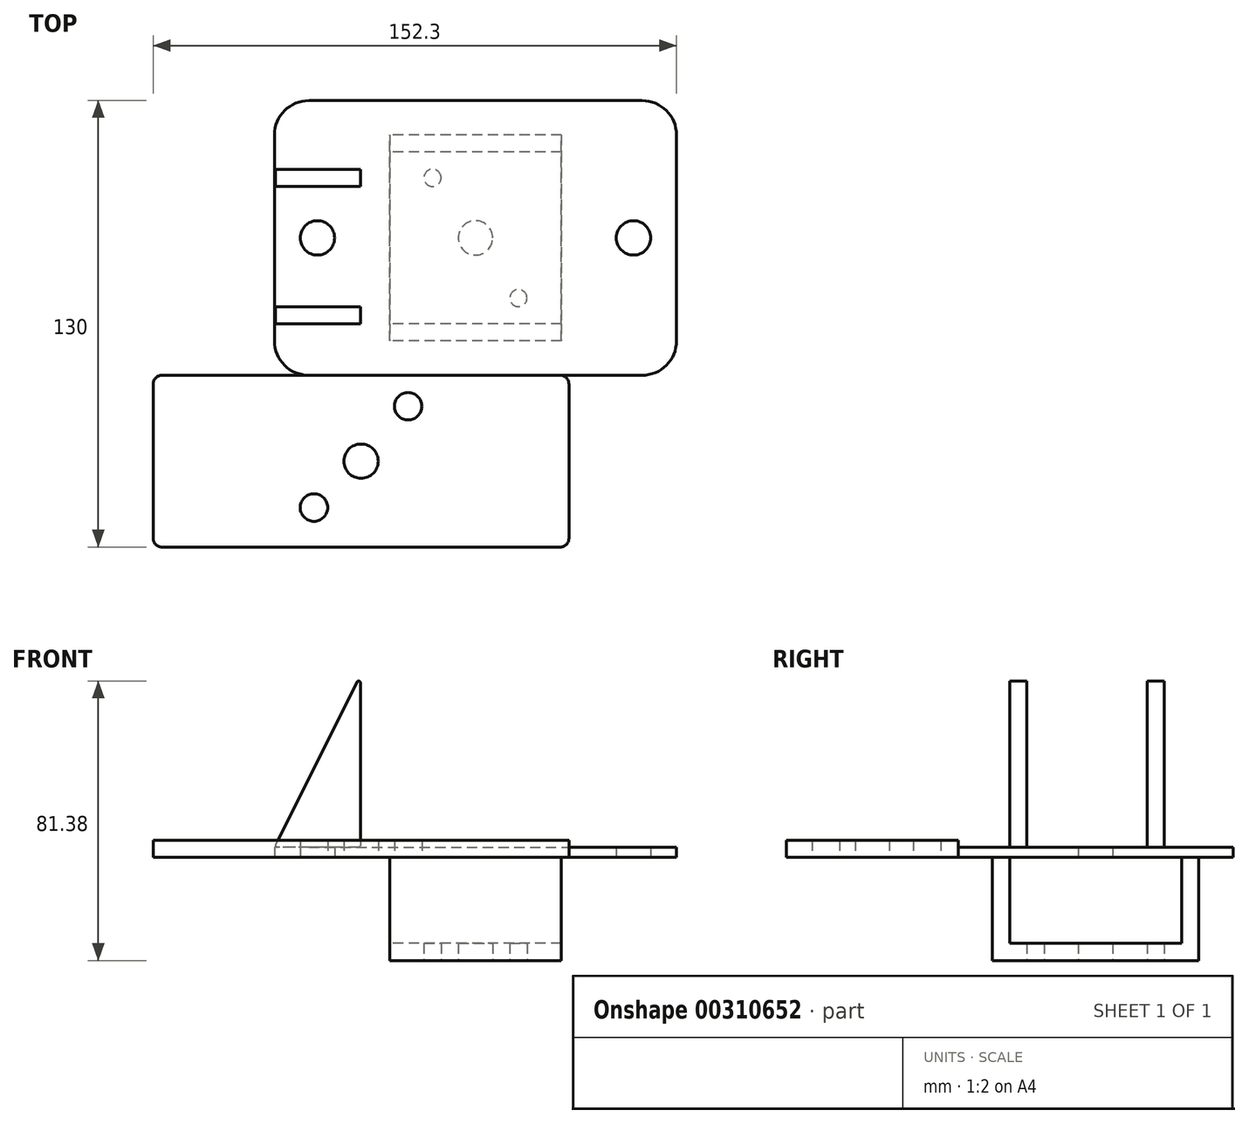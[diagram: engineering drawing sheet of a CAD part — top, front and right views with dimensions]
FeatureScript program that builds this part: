
annotation { "Feature Type Name" : "Feature", "Feature Type Description" : "" }
export const myFeature = defineFeature(function(context is Context, id is Id, definition is map)
    precondition{}
    {
        {
            var Q0;
            Q0=qCreatedBy(makeId("Top.planeOp"),FACE);
            var sketch = newSketch(context, id + "F0", { "sketchPlane" : qUnion([Q0])});
            skLineSegment(sketch, "E0.bottom", {"start": v(10, 0) * mm, "end": v(107, 0) * mm});
            skLineSegment(sketch, "E0.top", {"start": v(10, 80) * mm, "end": v(107, 80) * mm});
            skLineSegment(sketch, "E0.left", {"start": v(0, 10) * mm, "end": v(0, 70) * mm});
            skLineSegment(sketch, "E0.right", {"start": v(117, 10) * mm, "end": v(117, 70) * mm});
            skCircle(sketch, "E1", {"center": v(12.5, 40) * mm, "radius": 5 * mm});
            skCircle(sketch, "E2", {"center": v(104.5, 40) * mm, "radius": 5 * mm});
            skPoint(sketch, "E3", {"position": v(0, 40) * mm});
            skPoint(sketch, "E4.visualSharp", {"position": v(0, 80) * mm});
            skArc(sketch, "E4.filletArc", {"start": v(10, 80) * mm, "mid": v(2.93, 77.07) * mm, "end": v(0, 70) * mm});
            skPoint(sketch, "E5.visualSharp", {"position": v(117, 80) * mm});
            skArc(sketch, "E5.filletArc", {"start": v(117, 70) * mm, "mid": v(114.07, 77.07) * mm, "end": v(107, 80) * mm});
            skPoint(sketch, "E6.visualSharp", {"position": v(117, 0) * mm});
            skArc(sketch, "E6.filletArc", {"start": v(107, 0) * mm, "mid": v(114.07, 2.93) * mm, "end": v(117, 10) * mm});
            skPoint(sketch, "E7.visualSharp", {"position": v(0, 0) * mm});
            skArc(sketch, "E7.filletArc", {"start": v(0, 10) * mm, "mid": v(2.93, 2.93) * mm, "end": v(10, 0) * mm});
            skSolve(sketch);
        }
        {
            var Q0;
            Q0 = qSketchRegion(id + "F0", true);
            extrude(context, id + "F1", {"entities" : qUnion([Q0]), "depth" : 3 * mm});
        }
        {
            var Q0;
            Q0=qCreatedBy(makeId("Right.planeOp"),FACE);
            var sketch = newSketch(context, id + "F2", { "sketchPlane" : qUnion([Q0])});
            skLineSegment(sketch, "E8", {"start": v(10, 0) * mm, "end": v(10, -30) * mm});
            skLineSegment(sketch, "E9", {"start": v(10, -30) * mm, "end": v(70, -30) * mm});
            skLineSegment(sketch, "E10", {"start": v(70, -30) * mm, "end": v(70, 0) * mm});
            skLineSegment(sketch, "E11", {"start": v(70, 0) * mm, "end": v(65, 0) * mm});
            skLineSegment(sketch, "E12", {"start": v(65, 0) * mm, "end": v(65, -25) * mm});
            skLineSegment(sketch, "E13", {"start": v(65, -25) * mm, "end": v(15, -25) * mm});
            skLineSegment(sketch, "E14", {"start": v(15, -25) * mm, "end": v(15, 0) * mm});
            skLineSegment(sketch, "E15", {"start": v(15, 0) * mm, "end": v(10, 0) * mm});
            skSolve(sketch);
        }
        {
            var Q0;
            Q0 = qSketchRegion(id + "F2", true);
            extrude(context, id + "F3", {"entities" : qUnion([Q0]), "depth" : 50 * mm});
        }
        {
            var Q0;
            Q0=makeQuery(id+"F3.opExtrude","SWEPT_BODY",BODY,{"disambiguationData":[OSD([sQuery(id+"F2.wireOp",EDGE,"E8"),sQuery(id+"F2.wireOp",EDGE,"E9"),sQuery(id+"F2.wireOp",EDGE,"E10"),sQuery(id+"F2.wireOp",EDGE,"E11"),sQuery(id+"F2.wireOp",EDGE,"E12"),sQuery(id+"F2.wireOp",EDGE,"E13"),sQuery(id+"F2.wireOp",EDGE,"E14"),sQuery(id+"F2.wireOp",EDGE,"E15")])]});
            transform(context, id + "F4", {"entities" : qUnion([Q0]), "transformType" : TransformType.TRANSLATION_3D, "dx" : 33.5 * mm, "dy" : 0 * mm, "dz" : 0 * mm, "makeCopy" : false});
        }
        {
            var Q0;
            Q0=makeQuery(id+"F3.opExtrude","SWEPT_FACE",FACE,{"disambiguationData":[OSD([sQuery(id+"F2.wireOp",EDGE,"E9")])]});
            var sketch = newSketch(context, id + "F5", { "sketchPlane" : qUnion([Q0])});
            skCircle(sketch, "E16", {"center": v(58.5, -40) * mm, "radius": 5 * mm});
            skPoint(sketch, "E17", {"position": v(33.5, -40) * mm});
            skPoint(sketch, "E18", {"position": v(58.5, -10) * mm});
            skCircle(sketch, "E19", {"center": v(46, -57.5) * mm, "radius": 2.5 * mm});
            skCircle(sketch, "E20", {"center": v(71, -22.5) * mm, "radius": 2.5 * mm});
            skSolve(sketch);
        }
        {
            var Q0;
            Q0 = qSketchRegion(id + "F5", true);
            extrude(context, id + "F6", {"entities" : qUnion([Q0]), "operationType" : NewBodyOperationType.REMOVE, "oppositeDirection" : true, "depth" : 25 * mm});
        }
        {
            var Q0;
            Q0=qCreatedBy(makeId("Front.planeOp"),FACE);
            var sketch = newSketch(context, id + "F7", { "sketchPlane" : qUnion([Q0])});
            skLineSegment(sketch, "E21", {"start": v(25, 50.88) * mm, "end": v(25, 3.5) * mm});
            skLineSegment(sketch, "E22", {"start": v(24.5, 3) * mm, "end": v(0.8, 3) * mm});
            skLineSegment(sketch, "E23", {"start": v(0.36, 3.72) * mm, "end": v(24.05, 51.1) * mm});
            skPoint(sketch, "E24.visualSharp", {"position": v(25, 53) * mm});
            skArc(sketch, "E24.filletArc", {"start": v(25, 50.88) * mm, "mid": v(24.61, 51.37) * mm, "end": v(24.05, 51.1) * mm});
            skPoint(sketch, "E25.visualSharp", {"position": v(0, 3) * mm});
            skArc(sketch, "E25.filletArc", {"start": v(0.36, 3.72) * mm, "mid": v(0.38, 3.24) * mm, "end": v(0.8, 3) * mm});
            skPoint(sketch, "E26.visualSharp", {"position": v(25, 3) * mm});
            skArc(sketch, "E26.filletArc", {"start": v(24.5, 3) * mm, "mid": v(24.85, 3.15) * mm, "end": v(25, 3.5) * mm});
            skSolve(sketch);
        }
        {
            var Q0;
            Q0 = qSketchRegion(id + "F7", true);
            extrude(context, id + "F8", {"entities" : qUnion([Q0]), "depth" : 5 * mm});
        }
        {
            var Q0;
            Q0=makeQuery(id+"F8.opExtrude","SWEPT_BODY",BODY,{"disambiguationData":[OSD([sQuery(id+"F7.wireOp",EDGE,"E21"),sQuery(id+"F7.wireOp",EDGE,"E22"),sQuery(id+"F7.wireOp",EDGE,"E23"),sQuery(id+"F7.wireOp",EDGE,"E24.filletArc"),sQuery(id+"F7.wireOp",EDGE,"E25.filletArc"),sQuery(id+"F7.wireOp",EDGE,"E26.filletArc")])]});
            transform(context, id + "F9", {"entities" : qUnion([Q0]), "transformType" : TransformType.TRANSLATION_3D, "dx" : 0 * mm, "dy" : 20 * mm, "dz" : 0 * mm, "makeCopy" : false});
        }
        {
            var Q0;
            Q0=makeQuery(id+"F8.opExtrude","SWEPT_BODY",BODY,{"disambiguationData":[OSD([sQuery(id+"F7.wireOp",EDGE,"E21"),sQuery(id+"F7.wireOp",EDGE,"E22"),sQuery(id+"F7.wireOp",EDGE,"E23"),sQuery(id+"F7.wireOp",EDGE,"E24.filletArc"),sQuery(id+"F7.wireOp",EDGE,"E25.filletArc"),sQuery(id+"F7.wireOp",EDGE,"E26.filletArc")])]});
            transform(context, id + "F10", {"entities" : qUnion([Q0]), "transformType" : TransformType.TRANSLATION_3D, "dx" : 0 * mm, "dy" : 40 * mm, "dz" : 0 * mm, "makeCopy" : true});
        }
        {
            var Q0;
            Q0=qCreatedBy(makeId("Top.planeOp"),FACE);
            var sketch = newSketch(context, id + "F11", { "sketchPlane" : qUnion([Q0])});
            skLineSegment(sketch, "E27.bottom", {"start": v(0, 0) * mm, "end": v(50.4, 0) * mm});
            skLineSegment(sketch, "E27.top", {"start": v(0, -50) * mm, "end": v(50.4, -50) * mm});
            skLineSegment(sketch, "E27.left", {"start": v(0, 0) * mm, "end": v(0, -50) * mm});
            skLineSegment(sketch, "E27.right", {"start": v(50.4, 0) * mm, "end": v(50.4, -50) * mm});
            skCircle(sketch, "E28", {"center": v(25.2, -25) * mm, "radius": 5 * mm});
            skPoint(sketch, "E29", {"position": v(25.2, -50) * mm});
            skPoint(sketch, "E30", {"position": v(0, -25) * mm});
            skLineSegment(sketch, "E31.bottom", {"start": v(0, 0) * mm, "end": v(-32.8, 0) * mm});
            skLineSegment(sketch, "E31.top", {"start": v(0, -50) * mm, "end": v(-32.8, -50) * mm});
            skLineSegment(sketch, "E31.right", {"start": v(-35.3, -2.5) * mm, "end": v(-35.3, -47.5) * mm});
            skLineSegment(sketch, "E32.bottom", {"start": v(50.4, 0) * mm, "end": v(83.2, 0) * mm});
            skLineSegment(sketch, "E32.top", {"start": v(50.4, -50) * mm, "end": v(83.2, -50) * mm});
            skLineSegment(sketch, "E32.right", {"start": v(85.7, -2.5) * mm, "end": v(85.7, -47.5) * mm});
            skCircle(sketch, "E33", {"center": v(11.5, -38.5) * mm, "radius": 4 * mm});
            skCircle(sketch, "E34", {"center": v(38.9, -9) * mm, "radius": 4 * mm});
            skPoint(sketch, "E35.visualSharp", {"position": v(-35.3, -50) * mm});
            skArc(sketch, "E35.filletArc", {"start": v(-35.3, -47.5) * mm, "mid": v(-34.57, -49.27) * mm, "end": v(-32.8, -50) * mm});
            skPoint(sketch, "E36.visualSharp", {"position": v(-35.3, 0) * mm});
            skArc(sketch, "E36.filletArc", {"start": v(-32.8, 0) * mm, "mid": v(-34.57, -0.73) * mm, "end": v(-35.3, -2.5) * mm});
            skPoint(sketch, "E37.visualSharp", {"position": v(85.7, -50) * mm});
            skArc(sketch, "E37.filletArc", {"start": v(83.2, -50) * mm, "mid": v(84.97, -49.27) * mm, "end": v(85.7, -47.5) * mm});
            skPoint(sketch, "E38.visualSharp", {"position": v(85.7, 0) * mm});
            skArc(sketch, "E38.filletArc", {"start": v(85.7, -2.5) * mm, "mid": v(84.97, -0.73) * mm, "end": v(83.2, 0) * mm});
            skSolve(sketch);
        }
        {
            var Q0;
            Q0 = qSketchRegion(id + "F11", true);
            extrude(context, id + "F12", {"entities" : qUnion([Q0]), "depth" : 5 * mm});
        }
    });
